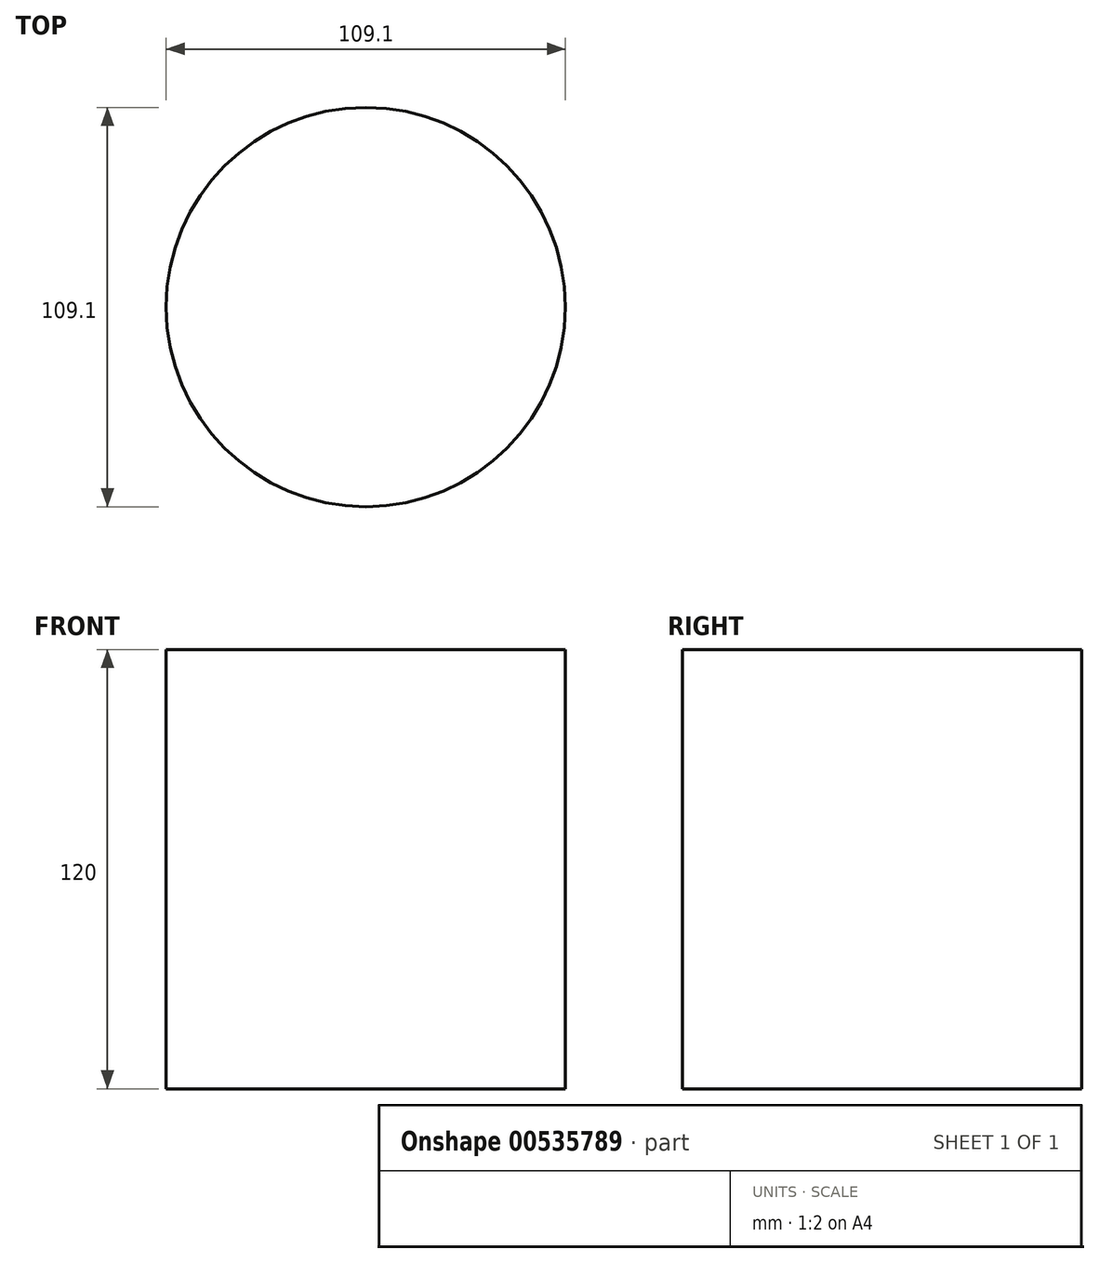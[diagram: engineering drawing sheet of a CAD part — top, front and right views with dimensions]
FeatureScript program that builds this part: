
annotation { "Feature Type Name" : "Feature", "Feature Type Description" : "" }
export const myFeature = defineFeature(function(context is Context, id is Id, definition is map)
    precondition{}
    {
        {
            var Q0;
            Q0=qCreatedBy(makeId("Top.planeOp"),FACE);
            var sketch = newSketch(context, id + "F0", { "sketchPlane" : qUnion([Q0])});
            skCircle(sketch, "E0", {"center": v(0, 0) * mm, "radius": 54.55 * mm});
            skSolve(sketch);
        }
        {
            var Q0;
            Q0 = qSketchRegion(id + "F0", true);
            extrude(context, id + "F1", {"entities" : qUnion([Q0]), "depth" : 120 * mm, "offsetDistance" : 25.4 * mm});
        }
    });
